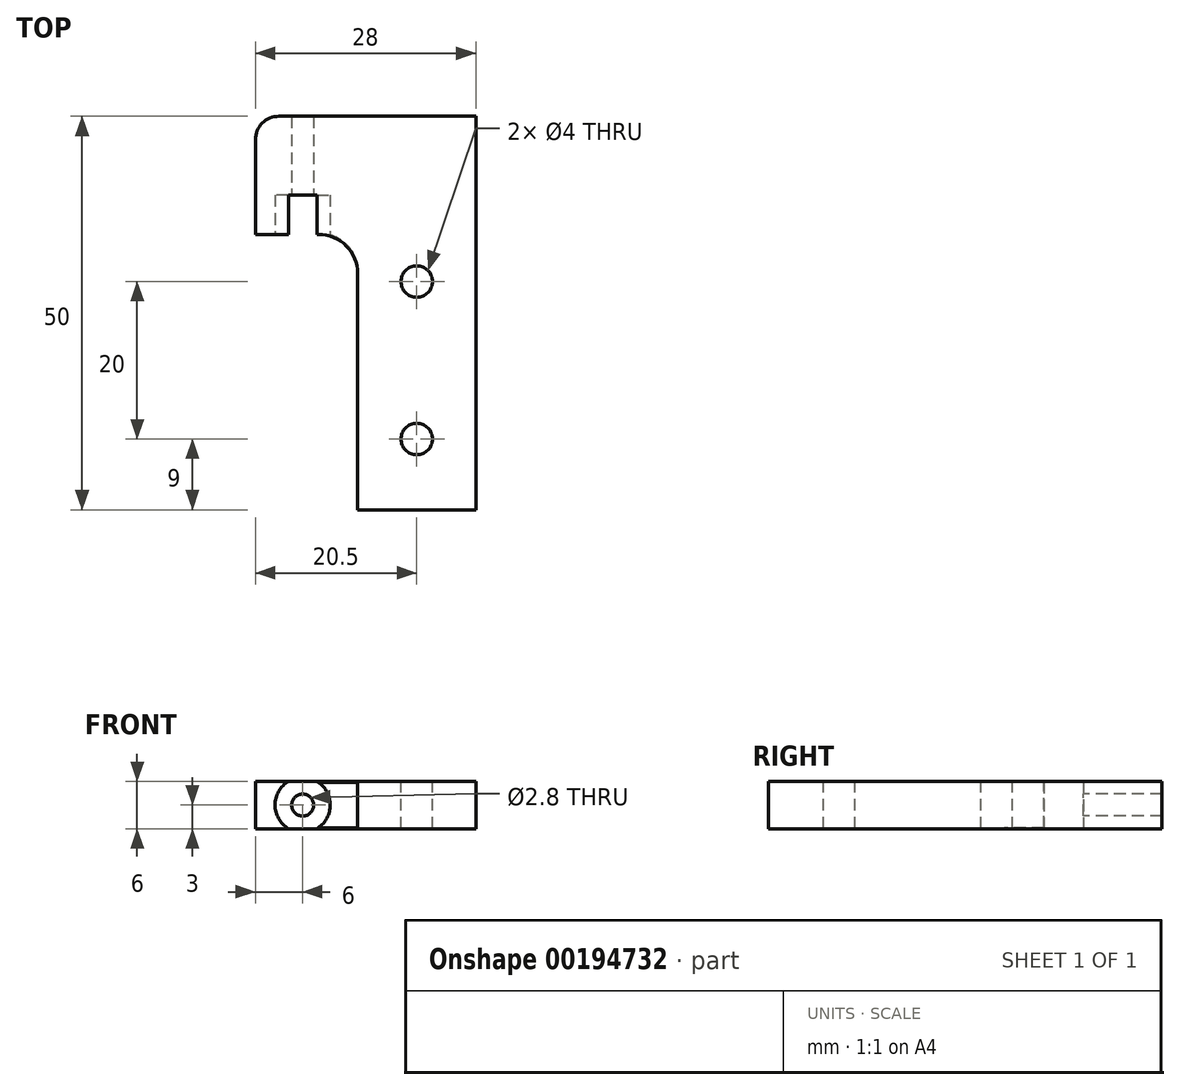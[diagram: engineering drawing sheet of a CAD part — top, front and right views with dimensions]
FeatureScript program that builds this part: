
annotation { "Feature Type Name" : "Feature", "Feature Type Description" : "" }
export const myFeature = defineFeature(function(context is Context, id is Id, definition is map)
    precondition{}
    {
        {
            var Q0;
            Q0=qCreatedBy(makeId("Top.planeOp"),FACE);
            var sketch = newSketch(context, id + "F0", { "sketchPlane" : qUnion([Q0])});
            skLineSegment(sketch, "E0", {"start": v(0, 50) * mm, "end": v(-25, 50) * mm});
            skLineSegment(sketch, "E1", {"start": v(-25, 50) * mm, "end": v(-25, 35) * mm});
            skLineSegment(sketch, "E2", {"start": v(0, 0) * mm, "end": v(-12, 0) * mm});
            skLineSegment(sketch, "E3", {"start": v(-12, 0) * mm, "end": v(-12, 30) * mm});
            skLineSegment(sketch, "E4", {"start": v(-17, 35) * mm, "end": v(-25, 35) * mm});
            skPoint(sketch, "E5.visualSharp", {"position": v(-12, 35) * mm});
            skLineSegment(sketch, "E6", {"start": v(0, 50) * mm, "end": v(3, 50) * mm});
            skLineSegment(sketch, "E7", {"start": v(3, 50) * mm, "end": v(3, 0) * mm});
            skLineSegment(sketch, "E8", {"start": v(3, 0) * mm, "end": v(0, 0) * mm});
            skLineSegment(sketch, "E9", {"start": v(-17, 35) * mm, "end": v(-12, 35) * mm});
            skLineSegment(sketch, "E10", {"start": v(-12, 30) * mm, "end": v(-12, 35) * mm});
            skSolve(sketch);
        }
        {
            var Q0;
            Q0 = qSketchRegion(id + "F0", true);
            extrude(context, id + "F1", {"entities" : qUnion([Q0]), "depth" : 6 * mm});
        }
        {
            var Q0;
            Q0=makeQuery(id+"F1.opExtrude","SWEPT_FACE",FACE,{"disambiguationData":[OSD([sQuery(id+"F0.wireOp",EDGE,"E0")])]});
            var sketch = newSketch(context, id + "F2", { "sketchPlane" : qUnion([Q0])});
            skLineSegment(sketch, "E11", {"start": v(25, 3) * mm, "end": v(44, 3) * mm});
            skCircle(sketch, "E12", {"center": v(44, 3) * mm, "radius": 1.4 * mm});
            skSolve(sketch);
        }
        {
            var Q0;
            Q0 = qSketchRegion(id + "F2", true);
            extrude(context, id + "F3", {"entities" : qUnion([Q0]), "operationType" : NewBodyOperationType.REMOVE, "oppositeDirection" : true, "depth" : 18 * mm});
        }
        {
            var Q0;
            Q0=makeQuery(id+"F1.opExtrude","SWEPT_FACE",FACE,{"disambiguationData":[OSD([sQuery(id+"F0.wireOp",EDGE,"E4")])]});
            var sketch = newSketch(context, id + "F4", { "sketchPlane" : qUnion([Q0])});
            skCircle(sketch, "E13", {"center": v(-19, 3) * mm, "radius": 3.5 * mm});
            skCircle(sketch, "E14", {"center": v(-19, 3) * mm, "radius": 1.4 * mm});
            skSolve(sketch);
        }
        {
            var Q0;
            Q0 = qSketchRegion(id + "F4", true);
            extrude(context, id + "F5", {"entities" : qUnion([Q0]), "operationType" : NewBodyOperationType.REMOVE, "oppositeDirection" : true, "depth" : 5 * mm});
        }
        {
            var Q0;
            Q0=makeQuery(id+"F1.opExtrude","CAP_FACE",FACE,{"disambiguationData":[OSD([sQuery(id+"F0.wireOp",EDGE,"tuEqIPry-F3bP-Fjx0-k920-EByhmmZksz2H"),sQuery(id+"F0.wireOp",EDGE,"E0"),sQuery(id+"F0.wireOp",EDGE,"E1"),sQuery(id+"F0.wireOp",EDGE,"E2"),sQuery(id+"F0.wireOp",EDGE,"E3"),sQuery(id+"F0.wireOp",EDGE,"E4"),sQuery(id+"F0.wireOp",EDGE,"E5.filletArc")])],"isStart":false});
            var sketch = newSketch(context, id + "F6", { "sketchPlane" : qUnion([Q0])});
            skLineSegment(sketch, "E15", {"start": v(-4.5, 0) * mm, "end": v(-4.5, 9) * mm});
            skLineSegment(sketch, "E16", {"start": v(-4.5, 9) * mm, "end": v(-4.5, 29) * mm});
            skCircle(sketch, "E17", {"center": v(-4.5, 29) * mm, "radius": 2 * mm});
            skCircle(sketch, "E18", {"center": v(-4.5, 9) * mm, "radius": 2 * mm});
            skSolve(sketch);
        }
        {
            var Q0;
            Q0 = qSketchRegion(id + "F6", true);
            extrude(context, id + "F7", {"entities" : qUnion([Q0]), "operationType" : NewBodyOperationType.REMOVE, "oppositeDirection" : true, "depth" : 10 * mm});
        }
        {
            var Q0;
            Q0=makeQuery(id+"F1.opExtrude","SWEPT_EDGE",EDGE,{"disambiguationData":[OSD([sQuery(id+"F0.wireOp",EDGE,"E0"),sQuery(id+"F0.wireOp",EDGE,"E1")])]});
            var Q1;
            Q1=makeQuery(id+"F1.opExtrude","SWEPT_EDGE",EDGE,{"disambiguationData":[OSD([sQuery(id+"F0.wireOp",EDGE,"tuEqIPry-F3bP-Fjx0-k920-EByhmmZksz2H"),sQuery(id+"F0.wireOp",EDGE,"E0")])]});
            fillet(context, id + "F8", {"entities" : qUnion([Q0, Q1]), "radius" : 3 * mm, "tangentPropagation" : true, "allowEdgeOverflow" : false});
        }
        {
            var Q0;
            Q0=makeQuery(id+"F1.opExtrude","SWEPT_EDGE",EDGE,{"disambiguationData":[OSD([sQuery(id+"F0.wireOp",EDGE,"E9"),sQuery(id+"F0.wireOp",EDGE,"E10")])]});
            fillet(context, id + "F9", {"entities" : qUnion([Q0]), "radius" : 5 * mm, "tangentPropagation" : true, "allowEdgeOverflow" : false});
        }
        {
            var Q0;
            Q0=makeQuery(id+"F5.boolean.opBoolean","SPLIT",FACE,{"disambiguationData":[TD([makeQuery(id+"F5.opExtrude","SWEPT_FACE",FACE,{"disambiguationData":[OSD([sQuery(id+"F4.wireOp",EDGE,"E14")])]})])],"derivedFrom":makeQuery(id+"F1.opExtrude","SWEPT_FACE",FACE,{"disambiguationData":[OSD([sQuery(id+"F0.wireOp",EDGE,"E4"),sQuery(id+"F0.wireOp",EDGE,"E9")])]})});
            extrude(context, id + "F10", {"entities" : qUnion([Q0]), "operationType" : NewBodyOperationType.REMOVE, "oppositeDirection" : true, "depth" : 25 * mm});
        }
    });
